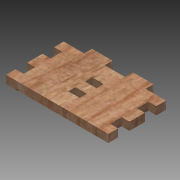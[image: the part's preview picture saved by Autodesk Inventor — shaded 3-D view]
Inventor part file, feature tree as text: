
AUTODESK INVENTOR PART (.ipt)
format: ipt  version: 2015 (Build 190159000, 159)  size: 274,432 bytes
history: native  units: mm
features: other x10, sketch x7, extrude x4
ambient origin geometry x8: Origin, YZ Plane, XZ Plane, XY Plane, X Axis, Y Axis, Z Axis, Center Point
bodies: Solid1 (feature_tree)
feature tree (21):
  other  "Blocks"
  extrude  "Extrusion1"  Depth=40.0mm
  sketch  "Sketch3"  dims[d2=5.5mm d3=0.0mm d16=5.5mm]
  extrude  "Extrusion4"  Depth=5.5mm
  extrude  "Extrusion5"  Depth=6.666667mm
  extrude  "Extrusion6"  Depth=5.0mm
  sketch  "Sketch16"  dims[d28=10.0mm d29=0.0mm]
  sketch  "Sketch17"  dims[d30=10.0mm d31=0.0mm d32=14.2mm d33=14.2mm d34=5.5mm d35=5.5mm d36=0.0mm]
  sketch  "Sketch15"  dims[d27=3.33mm]
  sketch  "Sketch1"  dims[d0=71.0mm d1=40.0mm]
  sketch  "Sketch4"  dims[d17=8.0mm d18=6.666667mm]
  sketch  "Sketch5"  dims[d25=8.0mm d26=5.0mm]
  other  "Block1"
  other  "Block2"
  other  "Block3"
  other  "Block4"
  other  "Block5"
  other  "Block4:1"
  other  "Block4:2"
  other  "Block5:1"
  other  "Block5:2"
